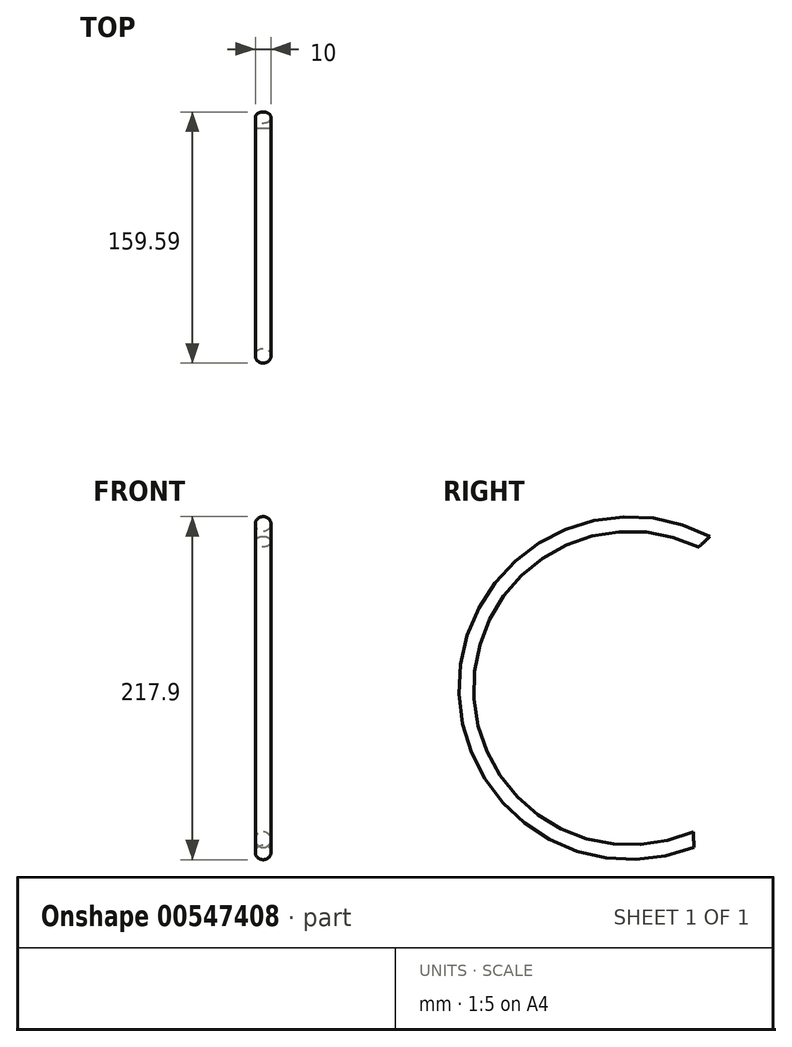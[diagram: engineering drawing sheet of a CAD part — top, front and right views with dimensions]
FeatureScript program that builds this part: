
annotation { "Feature Type Name" : "Feature", "Feature Type Description" : "" }
export const myFeature = defineFeature(function(context is Context, id is Id, definition is map)
    precondition{}
    {
        {
            var Q0;
            Q0=qCreatedBy(makeId("Front.planeOp"),FACE);
            var sketch = newSketch(context, id + "F0", { "sketchPlane" : qUnion([Q0])});
            skArc(sketch, "E0", {"start": v(-26.1, 96.54) * mm, "mid": v(-97.72, -21.24) * mm, "end": v(16.33, -98.66) * mm});
            skCircle(sketch, "E1", {"center": v(-99.5, 10) * mm, "radius": 5 * mm});
            skCircle(sketch, "E2.1.0", {"center": v(-97.72, -21.24) * mm, "radius": 5 * mm});
            skCircle(sketch, "E2.2.0", {"center": v(-86.37, -50.4) * mm, "radius": 5 * mm});
            skCircle(sketch, "E2.3.0", {"center": v(-66.57, -74.62) * mm, "radius": 5 * mm});
            skCircle(sketch, "E2.4.0", {"center": v(-40.26, -91.54) * mm, "radius": 5 * mm});
            skCircle(sketch, "E2.5.0", {"center": v(-10, -99.5) * mm, "radius": 5 * mm});
            skCircle(sketch, "E2.6.0", {"center": v(21.24, -97.72) * mm, "radius": 5 * mm});
            skCircle(sketch, "E2.7.0", {"center": v(50.4, -86.37) * mm, "radius": 5 * mm});
            skCircle(sketch, "E2.8.0", {"center": v(74.62, -66.57) * mm, "radius": 5 * mm});
            skCircle(sketch, "E2.9.0", {"center": v(91.54, -40.26) * mm, "radius": 5 * mm});
            skCircle(sketch, "E3.1.10.0", {"center": v(99.5, -10) * mm, "radius": 5 * mm});
            skCircle(sketch, "E3.1.11.0", {"center": v(97.72, 21.24) * mm, "radius": 5 * mm});
            skCircle(sketch, "E3.1.12.0", {"center": v(86.37, 50.4) * mm, "radius": 5 * mm});
            skCircle(sketch, "E3.1.13.0", {"center": v(66.57, 74.62) * mm, "radius": 5 * mm});
            skCircle(sketch, "E3.1.14.0", {"center": v(40.26, 91.54) * mm, "radius": 5 * mm});
            skCircle(sketch, "E3.1.15.0", {"center": v(10, 99.5) * mm, "radius": 5 * mm});
            skCircle(sketch, "E3.1.16.0", {"center": v(-21.24, 97.72) * mm, "radius": 5 * mm});
            skCircle(sketch, "E3.1.17.0", {"center": v(-50.4, 86.37) * mm, "radius": 5 * mm});
            skCircle(sketch, "E3.1.18.0", {"center": v(-74.62, 66.57) * mm, "radius": 5 * mm});
            skCircle(sketch, "E3.1.19.0", {"center": v(-91.54, 40.26) * mm, "radius": 5 * mm});
            skArc(sketch, "E4.trimOffspring", {"start": v(26.1, -96.54) * mm, "mid": v(97.72, 21.24) * mm, "end": v(-16.33, 98.66) * mm});
            skArc(sketch, "E5", {"start": v(99.5, -10) * mm, "mid": v(2.68, 26.66) * mm, "end": v(-99.5, 10) * mm});
            skSolve(sketch);
        }
        {
            var Q0;
            Q0=qCreatedBy(makeId("Top.planeOp"),FACE);
            var sketch = newSketch(context, id + "F1", { "sketchPlane" : qUnion([Q0])});
            skLineSegment(sketch, "E6", {"start": v(0.3, -1.32) * mm, "end": v(0.3, -36.32) * mm});
            skLineSegment(sketch, "E7", {"start": v(0.3, -36.32) * mm, "end": v(-53.76, -36.32) * mm});
            skLineSegment(sketch, "E8", {"start": v(-53.76, -36.32) * mm, "end": v(65.42, -36.32) * mm});
            skSolve(sketch);
        }
        {
            var Q0;
            {var subQ0=sQuery(id+"F0.wireOp",EDGE,"E2.6.0");var subQ1=makeQuery(id+"F0.imprint","INTERSECT",VERTEX,{"derivedFrom":[sQuery(id+"F0.wireOp",EDGE,"E0"),subQ0]});Q0=makeQuery(id+"F0.imprint","IMPRINT",FACE,{"disambiguationData":[TD([[makeQuery(id+"F0.imprint","IMPRINT",EDGE,{"disambiguationData":[TD([[subQ1,-1.0]])],"derivedFrom":subQ0}),1.0]])]});}
            var Q1;
            Q1=sQuery(id+"F1.wireOp",EDGE,"E8");
            revolve(context, id + "F2", {"entities" : qUnion([Q0]), "axis" : qUnion([Q1]), "revolveType" : RevolveType.TWO_DIRECTIONS, "oppositeDirection" : true, "angle" : 227.17 * degree, "angleBack" : 357.74 * degree});
        }
    });
